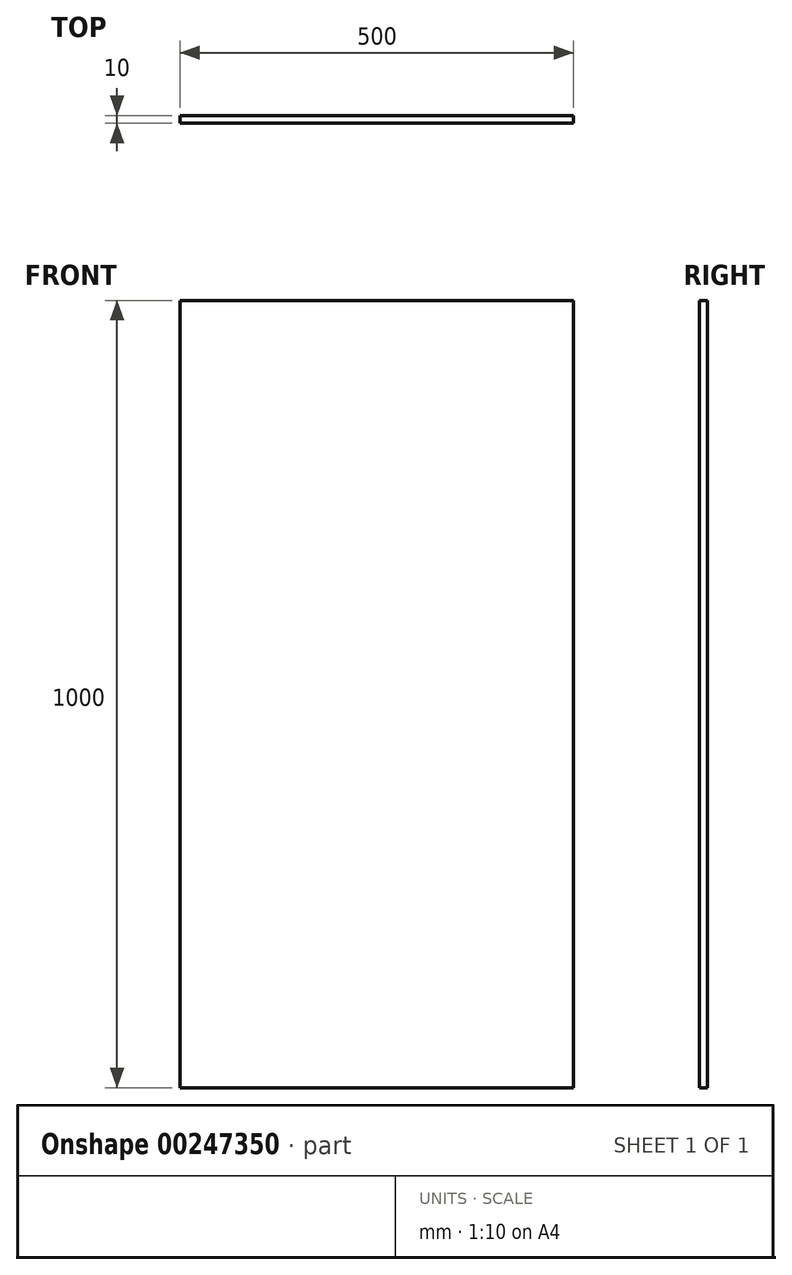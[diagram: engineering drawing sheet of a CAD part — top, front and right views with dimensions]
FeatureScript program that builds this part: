
annotation { "Feature Type Name" : "Feature", "Feature Type Description" : "" }
export const myFeature = defineFeature(function(context is Context, id is Id, definition is map)
    precondition{}
    {
        {
            var Q0;
            Q0=qCreatedBy(makeId("Front.planeOp"),FACE);
            var sketch = newSketch(context, id + "F0", { "sketchPlane" : qUnion([Q0])});
            skLineSegment(sketch, "E0.bottom", {"start": v(-327.34, 212.72) * mm, "end": v(172.66, 212.72) * mm});
            skLineSegment(sketch, "E0.top", {"start": v(-327.34, -787.28) * mm, "end": v(172.66, -787.28) * mm});
            skLineSegment(sketch, "E0.left", {"start": v(-327.34, 212.72) * mm, "end": v(-327.34, -787.28) * mm});
            skLineSegment(sketch, "E0.right", {"start": v(172.66, 212.72) * mm, "end": v(172.66, -787.28) * mm});
            skSolve(sketch);
        }
        {
            var Q0;
            Q0 = qSketchRegion(id + "F0", true);
            extrude(context, id + "F1", {"entities" : qUnion([Q0]), "depth" : 10 * mm});
        }
    });
